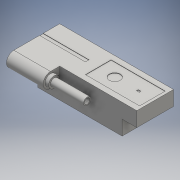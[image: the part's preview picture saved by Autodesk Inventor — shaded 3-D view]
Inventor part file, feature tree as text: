
AUTODESK INVENTOR PART (.ipt)
format: ipt  version: 2016 (Build 200138000, 138)  size: 195,072 bytes
history: native  units: mm
features: extrude x8, sketch x8, other x1, chamfer x1, thread x1
ambient origin geometry x8: Origin, YZ Plane, XZ Plane, XY Plane, X Axis, Y Axis, Z Axis, Center Point
bodies: Body1 (feature_tree)
feature tree (19):
  other  "ソリッド1"
  extrude  "押し出し1"  Depth=62.0mm
  extrude  "押し出し2"  Depth=20.0mm
  extrude  "押し出し3"  Depth=8.0mm TaperAngle=0.0deg
  extrude  "押し出し4"  Depth=1.0mm
  extrude  "押し出し5"  Depth=4.0mm
  chamfer  "面取り1"  Distance=6.0mm
  extrude  "押し出し6"  Depth=20.0mm TaperAngle=0.0deg
  extrude  "押し出し8"  Depth=2.0mm TaperAngle=0.0deg
  extrude  "押し出し9"  Depth=4.0mm
  thread  "ねじ1"
  sketch  "スケッチ1"
  sketch  "スケッチ2"
  sketch  "スケッチ3"
  sketch  "スケッチ4"
  sketch  "スケッチ5"
  sketch  "スケッチ6"
  sketch  "スケッチ7"
  sketch  "スケッチ9"
